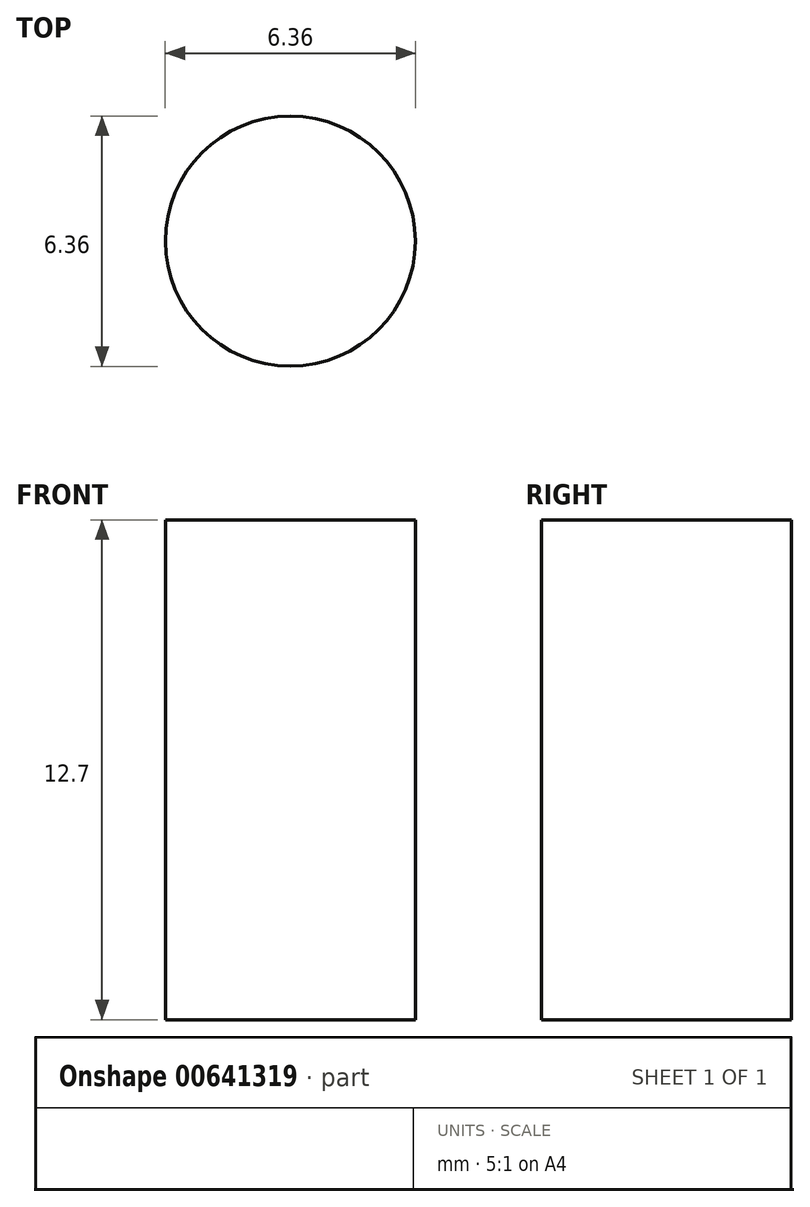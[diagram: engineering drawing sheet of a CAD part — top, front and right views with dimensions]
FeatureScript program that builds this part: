
annotation { "Feature Type Name" : "Feature", "Feature Type Description" : "" }
export const myFeature = defineFeature(function(context is Context, id is Id, definition is map)
    precondition{}
    {
        {
            var Q0;
            Q0=qCreatedBy(makeId("Front.planeOp"),FACE);
            var sketch = newSketch(context, id + "F0", { "sketchPlane" : qUnion([Q0])});
            skLineSegment(sketch, "E0", {"start": v(0, 0) * mm, "end": v(3.18, 0) * mm});
            skLineSegment(sketch, "E1", {"start": v(3.18, 0) * mm, "end": v(3.18, 12.7) * mm});
            skLineSegment(sketch, "E2", {"start": v(0, 12.7) * mm, "end": v(5.08, 12.7) * mm});
            skLineSegment(sketch, "E3", {"start": v(0, 0) * mm, "end": v(0, 16.51) * mm});
            skLineSegment(sketch, "E4", {"start": v(0, 16.51) * mm, "end": v(0, 11.23) * mm});
            skArc(sketch, "E5", {"start": v(0, 16.51) * mm, "mid": v(3.17, 15.45) * mm, "end": v(5.07, 12.7) * mm});
            skSolve(sketch);
        }
        {
            var Q0;
            {var subQ4=sQuery(id+"F0.wireOp",EDGE,"E5");Q0=makeQuery(id+"F0.imprint","IMPRINT",FACE,{"disambiguationData":[TD([[makeQuery(id+"F0.imprint","IMPRINT",EDGE,{"derivedFrom":subQ4}),-1.0]])]});}
            var Q1;
            Q1=makeQuery(id+"F0.imprint","IMPRINT",FACE,{"disambiguationData":[TD([[makeQuery(id+"F0.imprint","IMPRINT",EDGE,{"derivedFrom":sQuery(id+"F0.wireOp",EDGE,"E0")}),1.0]])]});
            var Q2;
            Q2=sQuery(id+"F0.wireOp",EDGE,"E3");
            revolve(context, id + "F1", {"entities" : qUnion([Q0, Q1]), "axis" : qUnion([Q2]), "revolveType" : RevolveType.FULL});
        }
    });
